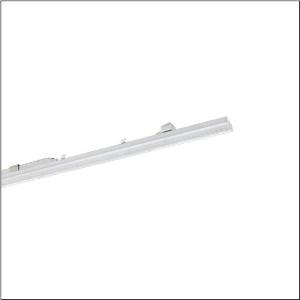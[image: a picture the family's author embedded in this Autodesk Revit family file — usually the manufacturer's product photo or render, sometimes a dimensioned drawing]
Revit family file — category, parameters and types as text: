
# Revit family: tl_l_5wd7a8d0h2c5
name_source: partatom
category: Lighting Fixtures
units: mm (PartAtom-declared; Revit-internal decimal feet)

## family parameters
Cut with Voids When Loaded = No
Host = Face
Light Source = No
Part Type = Normal
Room Calculation Point = No
Round Connector Dimension = Use Diameter
Shared = No

## types (1)
- --- (1 x LED, 9800 lm, 63.3 W, 4000K)
    Apparent Load = 63 VA
    CIE Flux Codes = 49 84 98 100 100
    Color Rendering = 80
    Color Temperature = 4000K
    Default Elevation = 1800 mm
    Description = TL L, luminaire insert, of sheet steel, galvanised, coil coated, white, length: 1.500mm, width: 66mm, height: 67mm, surge protection,LED rated luminous flux: 9.800lm, light colour: 840, control gear: DALI, with terminal, 5-pole, mains connection: 230..240V, AC, 50/60Hz, rated input power: 63W, micro fuse,primary optical cover: cover, of PMMA, light emission: direct distribution, protection rating (complete): as luminaire, insulation class (complete): insulation class I (protective earthing), certification: CE, impact resistance: IK06, permissible ambient temperature for indoor applications: -25..+35°C, packaging unit: 1 piece
    Height = 120 mm
    Lamp = 1 x LED
    Lamp Light Flux = 9800 lm
    Lamp Power = 63.3 W
    Lamp count = 1
    Length = 1690 mm
    Luminous efficacy = 155 lm/W
    Manufacturer = Siteco
    ModVariant = No
    Model = 5WD7A8D0H2C5
    Mounting Place = Ceiling
    Mounting Type = Pendant
    Number of Poles = 1
    OnlyDefault = Yes
    Power Factor = 1
    Product Name = TL L
    Product group = luminaire insert
    ProductGroupID = 901
    Protection Class = Protection class I
    Protection Degree = Degree of protection
    RLX_Detail_Level = 1
    RLX_Emergency_Light_Flux = 0 lm
    RLX_Emergency_Type = 0
    RLX_Emergency_Type_DB = No
    RlxData = <blob elided: 17357 chars, md5=967c0ce7>
    Socket = socket
    Standby Power = 0 W
    System Light Flux = 9800 lm
    System Power = 63 W
    Type Comments = factory setting: luminous flux: 100 % | dim-lin: 254 | 420 mA
    Type Image = l_1294382.jpg
    URL = http://relux.com
    VarID = @adj_031193
    Voltage = 0 V
    Weight = 0.00 kg
    Width = 208 mm

## geometry (parser evidence)
native form markers: Blend x4, Sweep x10
no freeform markers — native parametric forms only
